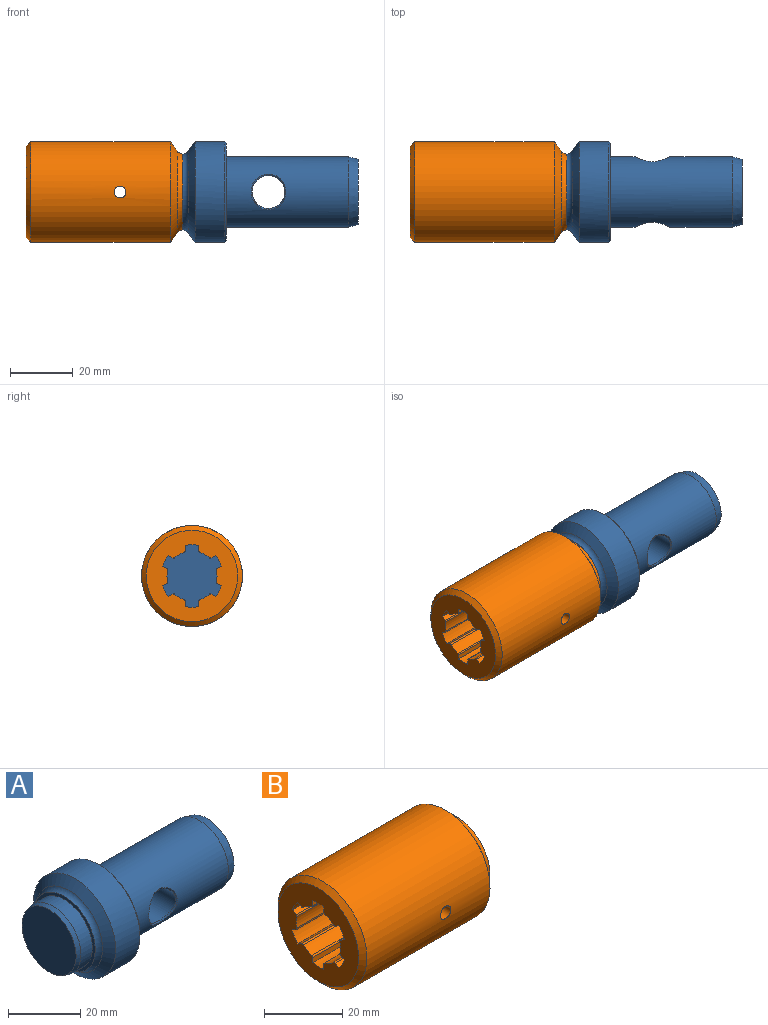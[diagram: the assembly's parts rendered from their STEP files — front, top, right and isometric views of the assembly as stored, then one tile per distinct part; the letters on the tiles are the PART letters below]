
ASSEMBLY  parts=2 mates=1
PART A: 15 faces, bbox 62x32.2x32.2 mm
  f0: plane 21.2x21.2mm, normal (-1,0,0), area 352.9mm2, adj f14
  f1: plane 20.89x20.89mm, normal (1,0,0), area 342.8mm2, adj f10
  f2: cylinder r=11.25mm len=39mm, axis (1,0,0), area 2550.3mm2, adj f3,f10,f12,f13
  f3: plane 31.2x31.2mm, normal (1,0,0), area 366.9mm2, adj f2,f11
  f4: cylinder r=16.1mm len=32.2mm, axis (1,0,0), area 961mm2, adj f5,f11
  f5: cone r=13.15mm half-angle=53.5deg, axis (1,0,0), area 337.4mm2, adj f4,f6
  f6: torus R=14.15mm, axis (1,0,0), area 172.4mm2, adj f5,f7
  f7: plane 24.2x24.2mm, normal (-1,0,0), area 79.8mm2, adj f6,f8
  f8: cylinder r=11mm len=22mm, axis (1,0,0), area 311mm2, adj f7,f14
  f9: cylinder r=5.25mm len=20.39mm, axis (0,-1,0), area 647.5mm2, adj f12,f13
  f10: cone r=10.45mm half-angle=15deg, axis (-1,0,0), area 211.7mm2, adj f1,f2
  f11: cone r=15.6mm half-angle=45deg, axis (-1,0,0), area 70.4mm2, adj f3,f4
  f12: bspline ~11.4x11.09mm, area 16.6mm2, adj f2,f9
  f13: bspline ~11.4x11.1mm, area 16.6mm2, adj f2,f9
  f14: cone r=11mm half-angle=15deg, axis (1,0,0), area 105.4mm2, adj f0,f8
PART B: 48 faces, bbox 50x32.2x32.2 mm
  f0: cylinder r=8mm len=13.42mm, axis (-1,0,0), area 45.5mm2, adj f8,f33,f36,f46
  f1: cylinder r=8mm len=13.42mm, axis (-1,0,0), area 45.5mm2, adj f8,f39,f41,f45
  f2: cylinder r=8mm len=44mm, axis (-1,0,0), area 160.6mm2, adj f8,f9,f42,f44
  f3: cylinder r=8mm len=44mm, axis (-1,0,0), area 160.6mm2, adj f8,f9,f34,f43
  f4: cylinder r=8mm len=29.42mm, axis (-1,0,0), area 103.9mm2, adj f9,f33,f36,f46
  f5: cylinder r=8mm len=44mm, axis (-1,0,0), area 160.6mm2, adj f8,f9,f35,f38
  f6: cylinder r=8mm len=44mm, axis (-1,0,0), area 160.6mm2, adj f8,f9,f37,f40
  f7: cylinder r=8mm len=29.42mm, axis (-1,0,0), area 103.9mm2, adj f9,f39,f41,f45
  f8: plane 22x22mm, normal (1,0,0), area 132.1mm2, adj f0,f1,f2,f3,f5,f6,f10,f15
  f9: plane 29.2x29.2mm, normal (-1,0,0), area 421.7mm2, adj f2,f3,f4,f5,f6,f7,f15,f16
  f10: cylinder r=11mm len=22mm, axis (-1,0,0), area 414.7mm2, adj f8,f11
  f11: plane 24.2x24.2mm, normal (1,0,0), area 79.8mm2, adj f10,f12
  f12: torus R=14.15mm, axis (-1,0,0), area 148.1mm2, adj f11,f13
  f13: cone r=16.1mm half-angle=53.7deg, axis (-1,0,0), area 358.1mm2, adj f12,f14
  f14: cylinder r=16.1mm len=44.54mm, axis (-1,0,0), area 4483.2mm2, adj f13,f45,f46,f47
  f15: cylinder r=9.95mm len=44mm, axis (-1,0,0), area 175mm2, adj f8,f9,f16,f17
  f16: plane 44x1.4mm, normal (0,-0.5,0.87), area 71.3mm2, adj f8,f9,f15,f41
  f17: plane 44x1.4mm, normal (0,0.5,-0.87), area 71.3mm2, adj f8,f9,f15,f42
  f18: cylinder r=9.95mm len=44mm, axis (-1,0,0), area 175mm2, adj f8,f9,f19,f20
  f19: plane 44x1.4mm, normal (0,0.5,0.87), area 71.3mm2, adj f8,f9,f18,f40
  f20: plane 44x1.4mm, normal (0,-0.5,-0.87), area 71.3mm2, adj f8,f9,f18,f39
  f21: cylinder r=9.95mm len=44mm, axis (-1,0,0), area 175mm2, adj f8,f9,f22,f23
  f22: plane 44x1.62mm, normal (0,1,0), area 71.3mm2, adj f8,f9,f21,f38
  f23: plane 44x1.62mm, normal (0,-1,0), area 71.3mm2, adj f8,f9,f21,f37
  f24: cylinder r=9.95mm len=44mm, axis (-1,0,0), area 175mm2, adj f8,f9,f25,f26
  f25: plane 44x1.4mm, normal (0,0.5,-0.87), area 71.3mm2, adj f8,f9,f24,f36
  f26: plane 44x1.4mm, normal (0,-0.5,0.87), area 71.3mm2, adj f8,f9,f24,f35
  f27: cylinder r=9.95mm len=44mm, axis (-1,0,0), area 175mm2, adj f8,f9,f28,f29
  f28: plane 44x1.4mm, normal (0,-0.5,-0.87), area 71.3mm2, adj f8,f9,f27,f34
  f29: plane 44x1.4mm, normal (0,0.5,0.87), area 71.3mm2, adj f8,f9,f27,f33
  f30: plane 44x1.62mm, normal (0,1,0), area 71.3mm2, adj f8,f9,f31,f43
  f31: cylinder r=9.95mm len=44mm, axis (-1,0,0), area 175mm2, adj f8,f9,f30,f32
  f32: plane 44x1.62mm, normal (0,-1,0), area 71.3mm2, adj f8,f9,f31,f44
  f33: cylinder r=0.5mm len=44mm, axis (-1,0,0), area 28mm2, adj f0,f4,f8,f9,f29,f46
  f34: cylinder r=0.5mm len=44mm, axis (-1,0,0), area 28.1mm2, adj f3,f8,f9,f28
  f35: cylinder r=0.5mm len=44mm, axis (-1,0,0), area 28.1mm2, adj f5,f8,f9,f26
  f36: cylinder r=0.5mm len=44mm, axis (-1,0,0), area 28mm2, adj f0,f4,f8,f9,f25,f46
  f37: cylinder r=0.5mm len=44mm, axis (-1,0,0), area 28.1mm2, adj f6,f8,f9,f23
  f38: cylinder r=0.5mm len=44mm, axis (-1,0,0), area 28.1mm2, adj f5,f8,f9,f22
  f39: cylinder r=0.5mm len=44mm, axis (-1,0,0), area 28mm2, adj f1,f7,f8,f9,f20,f45
  f40: cylinder r=0.5mm len=44mm, axis (-1,0,0), area 28.1mm2, adj f6,f8,f9,f19
  f41: cylinder r=0.5mm len=44mm, axis (-1,0,0), area 28mm2, adj f1,f7,f8,f9,f16,f45
  f42: cylinder r=0.5mm len=44mm, axis (-1,0,0), area 28.1mm2, adj f2,f8,f9,f17
  f43: cylinder r=0.5mm len=44mm, axis (-1,0,0), area 28.1mm2, adj f3,f8,f9,f30
  f44: cylinder r=0.5mm len=44mm, axis (-1,0,0), area 28.1mm2, adj f2,f8,f9,f32
  f45: cylinder r=1.9mm len=8.32mm, axis (0,-1,0), area 97.4mm2, adj f1,f7,f14,f39,f41
  f46: cylinder r=1.9mm len=8.32mm, axis (0,-1,0), area 97.4mm2, adj f0,f4,f14,f33,f36
  f47: cone r=14.6mm half-angle=45deg, axis (1,0,0), area 204.6mm2, adj f9,f14
PLACE A t=(50,0,0)mm
PLACE B t=(6,0,0)mm
MATE planar B.f0 <-> A.f2  axis (1,0,0) through (56,0,0)mm
